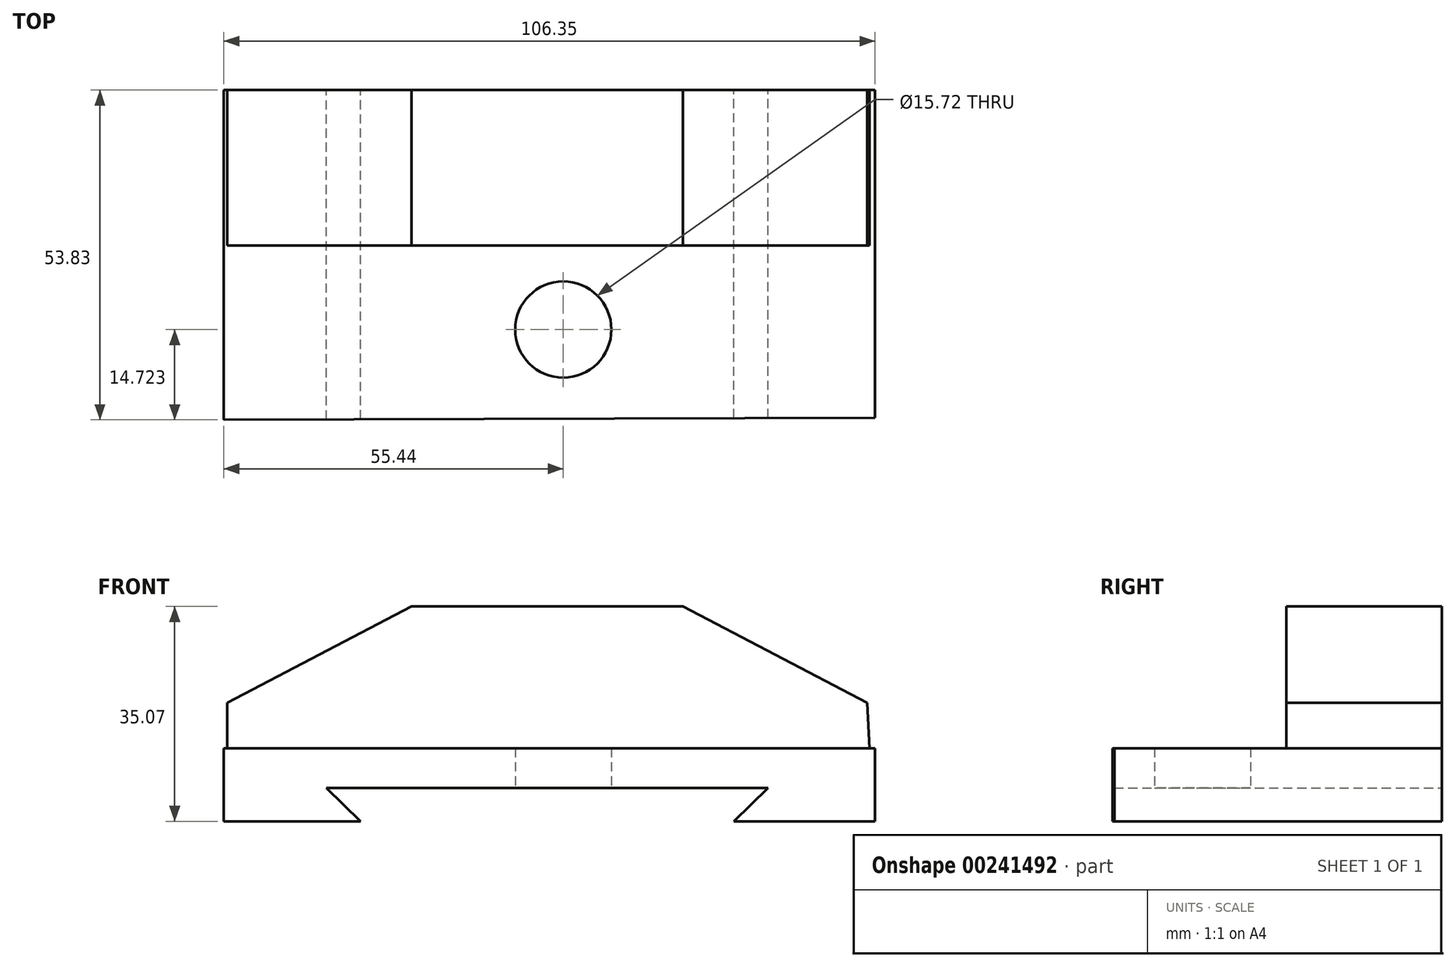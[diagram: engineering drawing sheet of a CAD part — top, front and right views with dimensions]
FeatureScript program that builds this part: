
annotation { "Feature Type Name" : "Feature", "Feature Type Description" : "" }
export const myFeature = defineFeature(function(context is Context, id is Id, definition is map)
    precondition{}
    {
        {
            var Q0;
            Q0=qCreatedBy(makeId("Front.planeOp"),FACE);
            var sketch = newSketch(context, id + "F0", { "sketchPlane" : qUnion([Q0])});
            skLineSegment(sketch, "E0", {"start": v(-54.88, 0) * mm, "end": v(50.58, 0) * mm});
            skLineSegment(sketch, "E1", {"start": v(-54.88, 0) * mm, "end": v(-54.88, 19.32) * mm});
            skLineSegment(sketch, "E2", {"start": v(-54.88, 19.32) * mm, "end": v(-24.82, 35.07) * mm});
            skLineSegment(sketch, "E3", {"start": v(-24.82, 35.07) * mm, "end": v(19.57, 35.07) * mm});
            skLineSegment(sketch, "E4", {"start": v(19.57, 35.07) * mm, "end": v(49.63, 19.32) * mm});
            skLineSegment(sketch, "E5", {"start": v(49.63, 19.32) * mm, "end": v(50.58, 0) * mm});
            skSolve(sketch);
        }
        {
            var Q0;
            Q0=qCreatedBy(makeId("Top.planeOp"),FACE);
            var sketch = newSketch(context, id + "F1", { "sketchPlane" : qUnion([Q0])});
            skLineSegment(sketch, "E6", {"start": v(-55.44, 0) * mm, "end": v(-55.44, -53.83) * mm});
            skLineSegment(sketch, "E7", {"start": v(50.91, 0) * mm, "end": v(50.91, -53.5) * mm});
            skLineSegment(sketch, "E8", {"start": v(-55.44, -53.83) * mm, "end": v(50.91, -53.5) * mm});
            skLineSegment(sketch, "E9", {"start": v(-55.44, 0) * mm, "end": v(50.91, 0) * mm});
            skSolve(sketch);
        }
        {
            var Q0;
            Q0=makeQuery(id+"F1.imprint","IMPRINT",FACE,{"disambiguationData":[TD([[makeQuery(id+"F1.imprint","IMPRINT",EDGE,{"derivedFrom":sQuery(id+"F1.wireOp",EDGE,"E6")}),1.0]])]});
            extrude(context, id + "F2", {"entities" : qUnion([Q0]), "depth" : 11.94 * mm});
        }
        {
            var Q0;
            Q0=makeQuery(id+"F0.imprint","IMPRINT",FACE,{"disambiguationData":[TD([[makeQuery(id+"F0.imprint","IMPRINT",EDGE,{"derivedFrom":sQuery(id+"F0.wireOp",EDGE,"E0")}),1.0]])]});
            extrude(context, id + "F3", {"entities" : qUnion([Q0]), "operationType" : NewBodyOperationType.ADD, "depth" : 25.4 * mm});
        }
        {
            var Q0;
            Q0=qCreatedBy(makeId("Front.planeOp"),FACE);
            var sketch = newSketch(context, id + "F4", { "sketchPlane" : qUnion([Q0])});
            skLineSegment(sketch, "E10", {"start": v(-38.7, 5.43) * mm, "end": v(-33.1, 0) * mm});
            skLineSegment(sketch, "E11", {"start": v(-38.7, 5.43) * mm, "end": v(33.44, 5.43) * mm});
            skLineSegment(sketch, "E12", {"start": v(33.44, 5.43) * mm, "end": v(27.84, 0) * mm});
            skLineSegment(sketch, "E13", {"start": v(-33.1, 0) * mm, "end": v(27.84, 0) * mm});
            skSolve(sketch);
        }
        {
            var Q0;
            Q0 = qSketchRegion(id + "F4", true);
            extrude(context, id + "F5", {"entities" : qUnion([Q0]), "operationType" : NewBodyOperationType.REMOVE, "depth" : 72.64 * mm});
        }
        {
            var Q0;
            Q0=qCreatedBy(makeId("Top.planeOp"),FACE);
            var sketch = newSketch(context, id + "F6", { "sketchPlane" : qUnion([Q0])});
            skCircle(sketch, "E14", {"center": v(0, -39.1) * mm, "radius": 7.86 * mm});
            skSolve(sketch);
        }
        {
            var Q0;
            Q0 = qSketchRegion(id + "F6", true);
            extrude(context, id + "F7", {"entities" : qUnion([Q0]), "operationType" : NewBodyOperationType.REMOVE, "depth" : 35.3 * mm});
        }
    });
